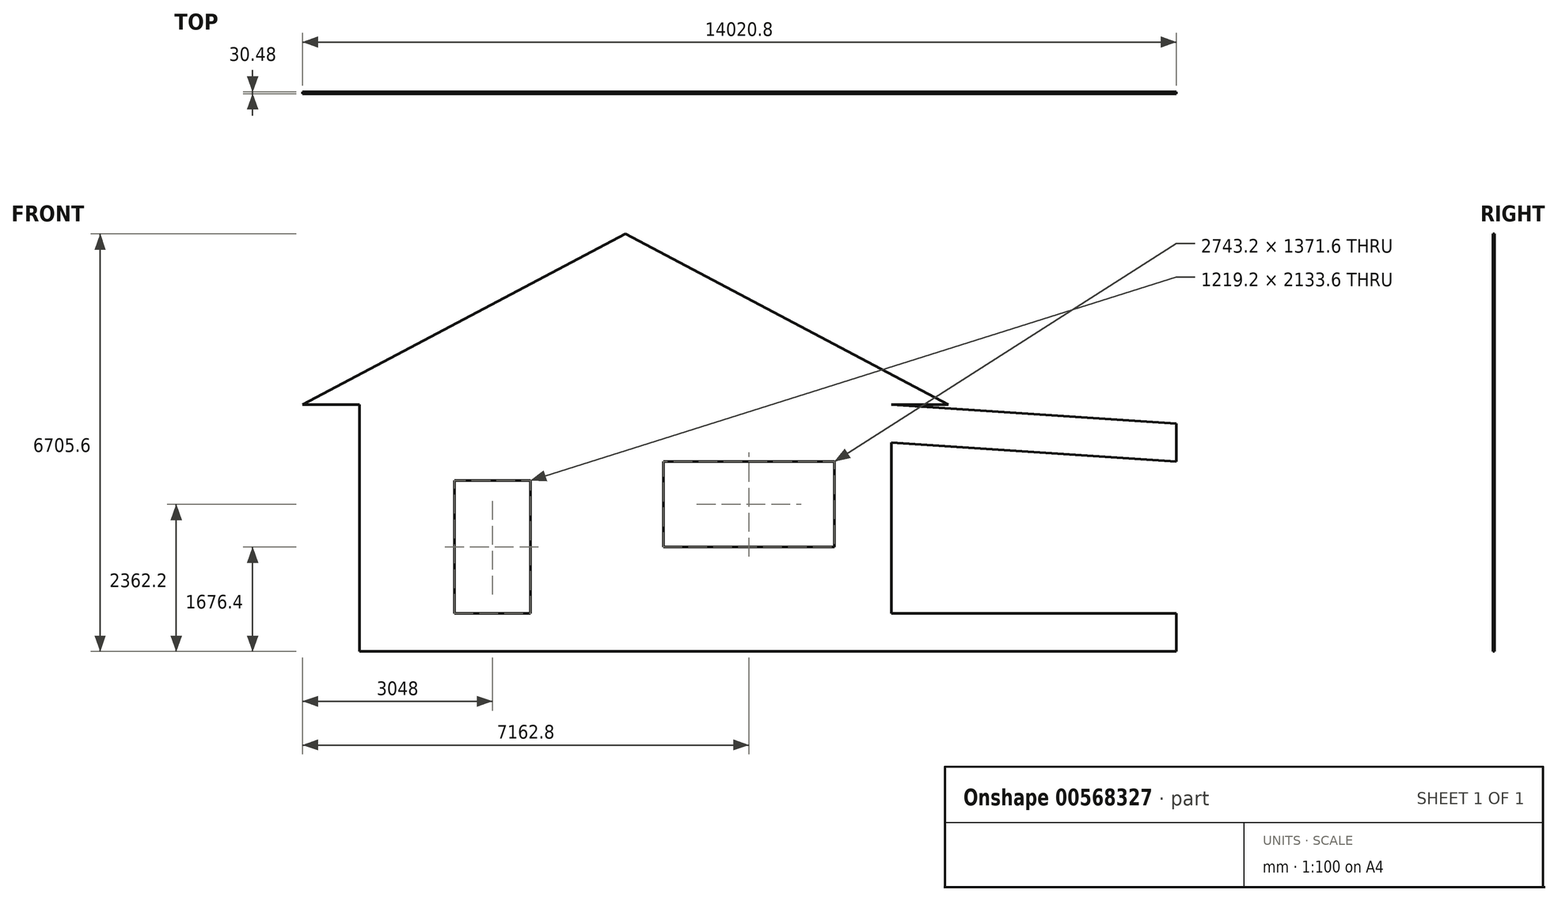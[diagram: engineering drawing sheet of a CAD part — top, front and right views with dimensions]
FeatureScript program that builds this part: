
annotation { "Feature Type Name" : "Feature", "Feature Type Description" : "" }
export const myFeature = defineFeature(function(context is Context, id is Id, definition is map)
    precondition{}
    {
        {
            var Q0;
            Q0=qCreatedBy(makeId("Front.planeOp"),FACE);
            var sketch = newSketch(context, id + "F0", { "sketchPlane" : qUnion([Q0])});
            skLineSegment(sketch, "E0", {"start": v(0, 0) * mm, "end": v(-4267.2, 0) * mm});
            skLineSegment(sketch, "E1", {"start": v(0, 0) * mm, "end": v(4267.2, 0) * mm});
            skLineSegment(sketch, "E2", {"start": v(0, 0) * mm, "end": v(0, 2286) * mm});
            skLineSegment(sketch, "E3", {"start": v(0, 2286) * mm, "end": v(0, 2743.2) * mm});
            skLineSegment(sketch, "E4", {"start": v(0, 2286) * mm, "end": v(-4267.2, 0) * mm});
            skLineSegment(sketch, "E5", {"start": v(0, 2286) * mm, "end": v(4267.2, 0) * mm});
            skLineSegment(sketch, "E6", {"start": v(-4267.2, 0) * mm, "end": v(-5181.6, 0) * mm});
            skLineSegment(sketch, "E7", {"start": v(4267.2, 0) * mm, "end": v(5181.6, 0) * mm});
            skLineSegment(sketch, "E8", {"start": v(0, 2743.2) * mm, "end": v(-5181.6, 0) * mm});
            skLineSegment(sketch, "E9", {"start": v(0, 2743.2) * mm, "end": v(5181.6, 0) * mm});
            skLineSegment(sketch, "E10", {"start": v(-4267.2, 0) * mm, "end": v(-4267.2, -3352.8) * mm});
            skLineSegment(sketch, "E11", {"start": v(-4267.2, -3352.8) * mm, "end": v(4267.2, -3352.8) * mm});
            skLineSegment(sketch, "E12", {"start": v(4267.2, 0) * mm, "end": v(4267.2, -3352.8) * mm});
            skLineSegment(sketch, "E13", {"start": v(4267.2, -3352.8) * mm, "end": v(8839.2, -3352.8) * mm});
            skLineSegment(sketch, "E14", {"start": v(8839.2, -3352.8) * mm, "end": v(8839.2, -914.4) * mm});
            skLineSegment(sketch, "E15", {"start": v(4267.2, 0) * mm, "end": v(4267.2, -609.6) * mm});
            skLineSegment(sketch, "E16", {"start": v(4267.2, -609.6) * mm, "end": v(8839.2, -914.4) * mm});
            skLineSegment(sketch, "E17", {"start": v(8839.2, -914.4) * mm, "end": v(8839.2, -304.8) * mm});
            skLineSegment(sketch, "E18", {"start": v(4267.2, 0) * mm, "end": v(8839.2, -304.8) * mm});
            skLineSegment(sketch, "E19", {"start": v(-4267.2, -3352.8) * mm, "end": v(-4267.2, -3962.4) * mm});
            skLineSegment(sketch, "E20", {"start": v(-4267.2, -3962.4) * mm, "end": v(4267.2, -3962.4) * mm});
            skLineSegment(sketch, "E21", {"start": v(4267.2, -3352.8) * mm, "end": v(4267.2, -3962.4) * mm});
            skLineSegment(sketch, "E22", {"start": v(4267.2, -3962.4) * mm, "end": v(8839.2, -3962.4) * mm});
            skLineSegment(sketch, "E23", {"start": v(8839.2, -3962.4) * mm, "end": v(8839.2, -3352.8) * mm});
            skLineSegment(sketch, "E24", {"start": v(-1524, -3352.8) * mm, "end": v(-1524, -1219.2) * mm});
            skLineSegment(sketch, "E25", {"start": v(-1524, -1219.2) * mm, "end": v(-2743.2, -1219.2) * mm});
            skLineSegment(sketch, "E26", {"start": v(-2743.2, -1219.2) * mm, "end": v(-2743.2, -3352.8) * mm});
            skLineSegment(sketch, "E27.bottom", {"start": v(609.6, -914.4) * mm, "end": v(3352.8, -914.4) * mm});
            skLineSegment(sketch, "E27.top", {"start": v(609.6, -2286) * mm, "end": v(3352.8, -2286) * mm});
            skLineSegment(sketch, "E27.left", {"start": v(609.6, -914.4) * mm, "end": v(609.6, -2286) * mm});
            skLineSegment(sketch, "E27.right", {"start": v(3352.8, -914.4) * mm, "end": v(3352.8, -2286) * mm});
            skLineSegment(sketch, "E28.bottom", {"start": v(5394.96, -1645.92) * mm, "end": v(6918.96, -1645.92) * mm});
            skLineSegment(sketch, "E28.top", {"start": v(5394.96, -2560.32) * mm, "end": v(6918.96, -2560.32) * mm});
            skLineSegment(sketch, "E28.left", {"start": v(5394.96, -1645.92) * mm, "end": v(5394.96, -2560.32) * mm});
            skLineSegment(sketch, "E28.right", {"start": v(6918.96, -1645.92) * mm, "end": v(6918.96, -2560.32) * mm});
            skLineSegment(sketch, "E29", {"start": v(-1219.2, -3352.8) * mm, "end": v(-1219.2, -914.4) * mm});
            skLineSegment(sketch, "E30", {"start": v(-1219.2, -914.4) * mm, "end": v(-3048, -914.4) * mm});
            skLineSegment(sketch, "E31", {"start": v(-3048, -914.4) * mm, "end": v(-3048, -3352.8) * mm});
            skText(sketch, "E32", { "text": "AUSTIN", "fontName": "OpenSans-Regular.ttf"});
            const initialGuessF0  = {"E32": [-4.13569, 2.95833, 1, 0, 1.8172]};
            skSetInitialGuess(sketch, initialGuessF0);
            skSolve(sketch);
        }
        {
            var Q0;
            Q0=makeQuery(id+"F0.imprint","IMPRINT",FACE,{"disambiguationData":[TD([[makeQuery(id+"F0.imprint","IMPRINT",EDGE,{"derivedFrom":sQuery(id+"F0.wireOp",EDGE,"E3")}),1.0]])]});
            var Q1;
            Q1=makeQuery(id+"F0.imprint","IMPRINT",FACE,{"disambiguationData":[TD([[makeQuery(id+"F0.imprint","IMPRINT",EDGE,{"derivedFrom":sQuery(id+"F0.wireOp",EDGE,"E3")}),-1.0]])]});
            var Q2;
            Q2=makeQuery(id+"F0.imprint","IMPRINT",FACE,{"disambiguationData":[TD([[makeQuery(id+"F0.imprint","IMPRINT",EDGE,{"derivedFrom":sQuery(id+"F0.wireOp",EDGE,"E0")}),-1.0]])]});
            var Q3;
            Q3=makeQuery(id+"F0.imprint","IMPRINT",FACE,{"disambiguationData":[TD([[makeQuery(id+"F0.imprint","IMPRINT",EDGE,{"derivedFrom":sQuery(id+"F0.wireOp",EDGE,"E1")}),1.0]])]});
            var Q4;
            Q4=makeQuery(id+"F0.imprint","IMPRINT",FACE,{"disambiguationData":[TD([[makeQuery(id+"F0.imprint","IMPRINT",EDGE,{"derivedFrom":sQuery(id+"F0.wireOp",EDGE,"E0")}),1.0]])]});
            var Q5;
            Q5=makeQuery(id+"F0.imprint","IMPRINT",FACE,{"disambiguationData":[TD([[makeQuery(id+"F0.imprint","IMPRINT",EDGE,{"derivedFrom":sQuery(id+"F0.wireOp",EDGE,"E15")}),1.0]])]});
            var Q6;
            Q6=makeQuery(id+"F0.imprint","IMPRINT",FACE,{"disambiguationData":[TD([[makeQuery(id+"F0.imprint","IMPRINT",EDGE,{"derivedFrom":sQuery(id+"F0.wireOp",EDGE,"E12")}),1.0]])]});
            var Q7;
            {var subQ6=sQuery(id+"F0.wireOp",EDGE,"E19");Q7=makeQuery(id+"F0.imprint","IMPRINT",FACE,{"disambiguationData":[TD([[makeQuery(id+"F0.imprint","IMPRINT",EDGE,{"derivedFrom":subQ6}),1.0]])]});}
            var Q8;
            Q8=makeQuery(id+"F0.imprint","IMPRINT",FACE,{"disambiguationData":[TD([[makeQuery(id+"F0.imprint","IMPRINT",EDGE,{"derivedFrom":sQuery(id+"F0.wireOp",EDGE,"E13")}),-1.0]])]});
            var Q9;
            {var subQ0=sQuery(id+"F0.wireOp",EDGE,"E24");Q9=makeQuery(id+"F0.imprint","IMPRINT",FACE,{"disambiguationData":[TD([[makeQuery(id+"F0.imprint","IMPRINT",EDGE,{"derivedFrom":subQ0}),-1.0]])]});}
            extrude(context, id + "F1", {"entities" : qUnion([Q0, Q1, Q2, Q3, Q4, Q5, Q6, Q7, Q8, Q9]), "depth" : 30.48 * mm, "offsetDistance" : 30.48 * mm});
        }
    });
